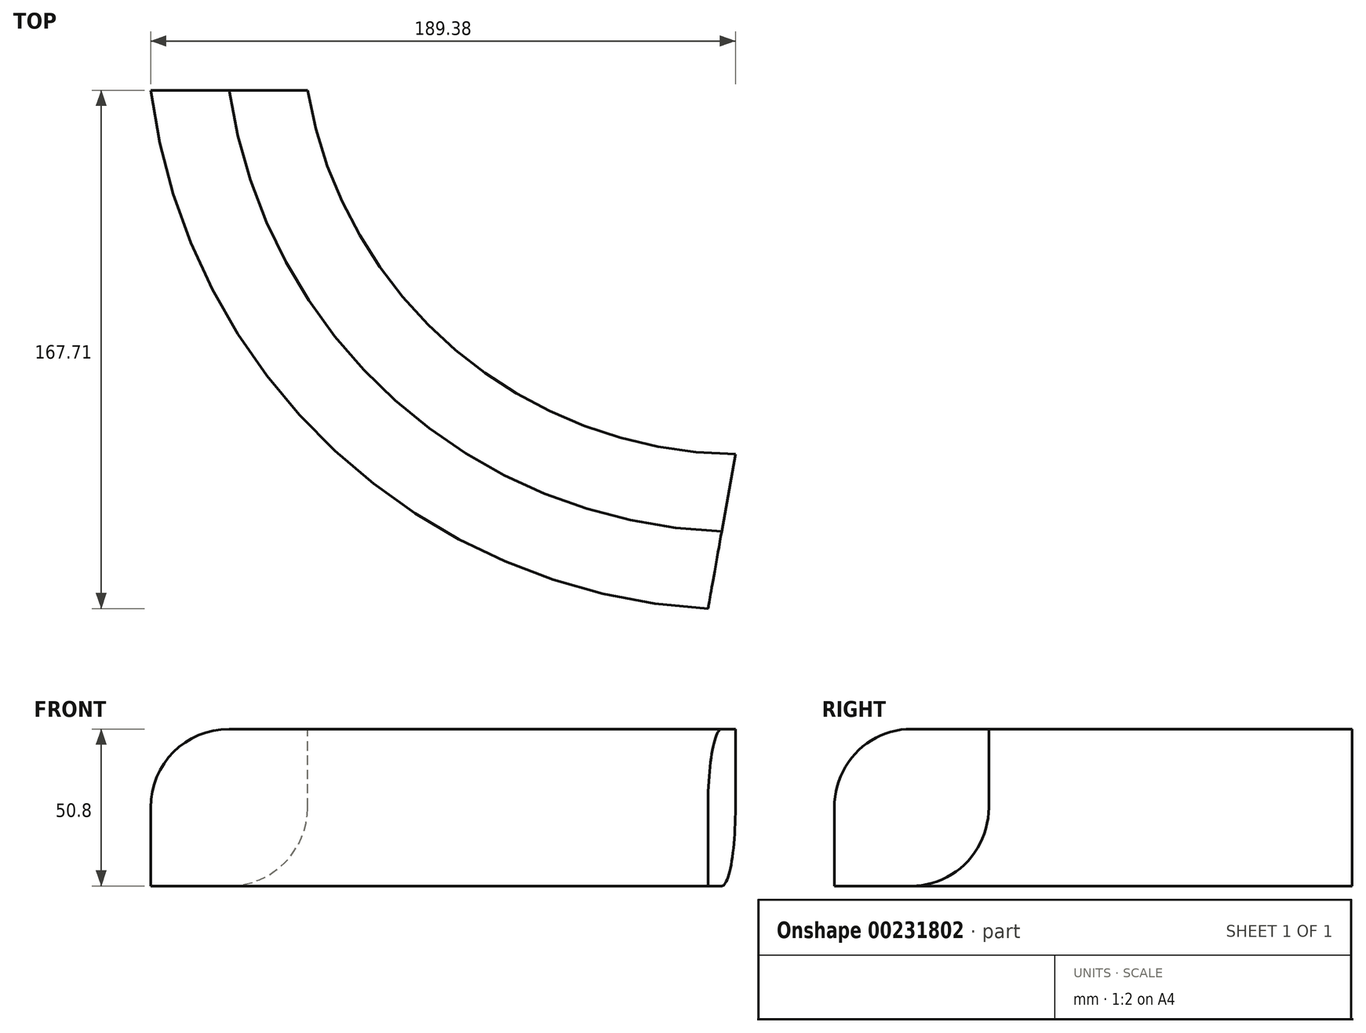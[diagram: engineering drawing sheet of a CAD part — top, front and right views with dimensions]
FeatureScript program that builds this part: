
annotation { "Feature Type Name" : "Feature", "Feature Type Description" : "" }
export const myFeature = defineFeature(function(context is Context, id is Id, definition is map)
    precondition{}
    {
        {
            var Q0;
            Q0=qCreatedBy(makeId("Front.planeOp"),FACE);
            var sketch = newSketch(context, id + "F0", { "sketchPlane" : qUnion([Q0])});
            skArc(sketch, "E0", {"start": v(-12.2, -14.4) * mm, "mid": v(5.75, -6.96) * mm, "end": v(13.2, 11) * mm});
            skLineSegment(sketch, "E1.bottom", {"start": v(-12.2, -14.4) * mm, "end": v(-37.6, -14.4) * mm});
            skLineSegment(sketch, "E1.top", {"start": v(13.2, 36.4) * mm, "end": v(-12.2, 36.4) * mm});
            skLineSegment(sketch, "E1.left", {"start": v(13.2, 11) * mm, "end": v(13.2, 36.4) * mm});
            skLineSegment(sketch, "E1.right", {"start": v(-37.6, -14.4) * mm, "end": v(-37.6, 11) * mm});
            skArc(sketch, "E2.trimOffspring", {"start": v(-12.2, 36.4) * mm, "mid": v(-30.17, 28.96) * mm, "end": v(-37.6, 11) * mm});
            skSolve(sketch);
        }
        {
            var Q0;
            Q0=qCreatedBy(makeId("Top.planeOp"),FACE);
            var sketch = newSketch(context, id + "F1", { "sketchPlane" : qUnion([Q0])});
            skArc(sketch, "E3", {"start": v(0, 0) * mm, "mid": v(50.97, -92.51) * mm, "end": v(149.46, -130.69) * mm});
            skSolve(sketch);
        }
        {
            var Q0;
            Q0=makeQuery(id+"F0.imprint","IMPRINT",FACE,{"disambiguationData":[TD([[makeQuery(id+"F0.imprint","IMPRINT",EDGE,{"derivedFrom":sQuery(id+"F0.wireOp",EDGE,"E0")}),1.0]])]});
            var Q1;
            Q1=sQuery(id+"F1.wireOp",EDGE,"E3");
            sweep(context, id + "F2", {"profiles" : qUnion([Q0]), "path" : qUnion([Q1])});
        }
    });
